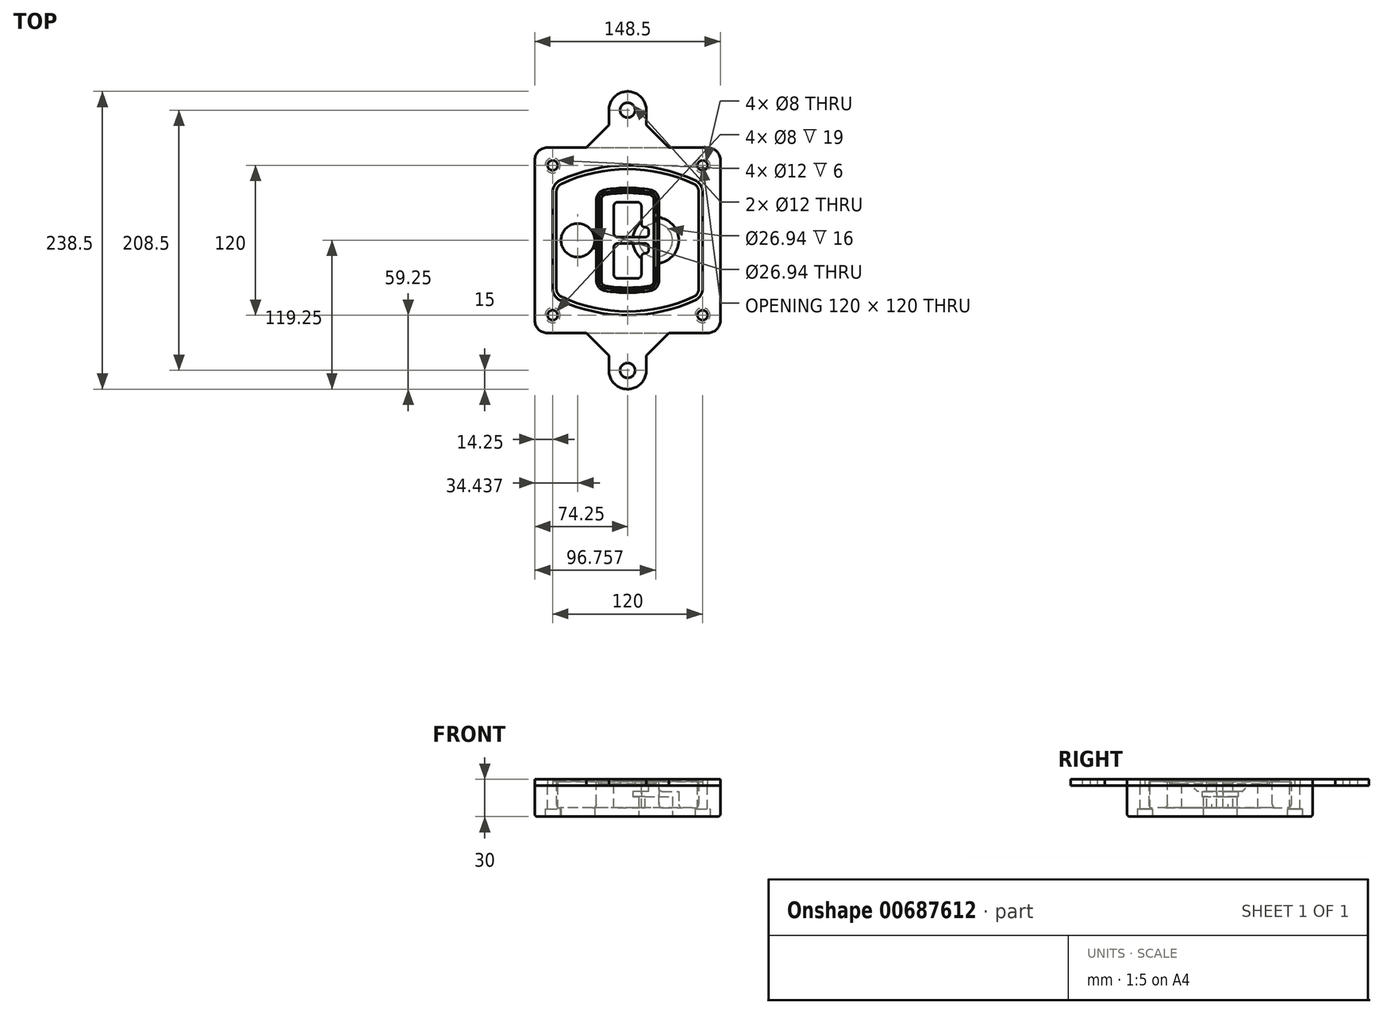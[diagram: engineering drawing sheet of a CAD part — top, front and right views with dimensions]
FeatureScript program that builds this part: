
annotation { "Feature Type Name" : "Feature", "Feature Type Description" : "" }
export const myFeature = defineFeature(function(context is Context, id is Id, definition is map)
    precondition{}
    {
        {
            var Q0;
            Q0=qCreatedBy(makeId("Top.planeOp"),FACE);
            var sketch = newSketch(context, id + "F0", { "sketchPlane" : qUnion([Q0])});
            skPoint(sketch, "E0.rect.middle", {"position": v(0, 0) * mm});
            skLineSegment(sketch, "E1.bottom", {"start": v(-64.25, -74.25) * mm, "end": v(64.25, -74.25) * mm});
            skLineSegment(sketch, "E1.top", {"start": v(-64.25, 74.25) * mm, "end": v(64.25, 74.25) * mm});
            skLineSegment(sketch, "E1.left", {"start": v(-74.25, -64.25) * mm, "end": v(-74.25, 64.25) * mm});
            skLineSegment(sketch, "E1.right", {"start": v(74.25, -64.25) * mm, "end": v(74.25, 64.25) * mm});
            skLineSegment(sketch, "E2", {"start": v(-74.25, 74.25) * mm, "end": v(74.25, -74.25) * mm, "construction": true});
            skLineSegment(sketch, "E3", {"start": v(74.25, 74.25) * mm, "end": v(-74.25, -74.25) * mm, "construction": true});
            skCircle(sketch, "E4", {"center": v(-60, 60) * mm, "radius": 4 * mm});
            skCircle(sketch, "E5", {"center": v(60, 60) * mm, "radius": 4 * mm});
            skCircle(sketch, "E6", {"center": v(60, -60) * mm, "radius": 4 * mm});
            skCircle(sketch, "E7", {"center": v(-60, -60) * mm, "radius": 4 * mm});
            skLineSegment(sketch, "E8", {"start": v(-60, 60) * mm, "end": v(60, 60) * mm, "construction": true});
            skLineSegment(sketch, "E9", {"start": v(60, 60) * mm, "end": v(60, -60) * mm, "construction": true});
            skLineSegment(sketch, "E10", {"start": v(60, -60) * mm, "end": v(-60, -60) * mm, "construction": true});
            skLineSegment(sketch, "E11", {"start": v(-60, -60) * mm, "end": v(-60, 60) * mm, "construction": true});
            skLineSegment(sketch, "E12", {"start": v(-60, 38.83) * mm, "end": v(-60, -38.83) * mm});
            skLineSegment(sketch, "E13", {"start": v(60, 38.83) * mm, "end": v(60, -38.83) * mm});
            skArc(sketch, "E14", {"start": v(54.26, 47.88) * mm, "mid": v(0, 60) * mm, "end": v(-54.26, 47.88) * mm});
            skArc(sketch, "E15", {"start": v(-54.26, -47.88) * mm, "mid": v(0, -60) * mm, "end": v(54.26, -47.88) * mm});
            skLineSegment(sketch, "E16", {"start": v(-60, 0) * mm, "end": v(60, 0) * mm, "construction": true});
            skPoint(sketch, "E17.visualSharp", {"position": v(-60, -45) * mm});
            skArc(sketch, "E17.filletArc", {"start": v(-60, -38.83) * mm, "mid": v(-58.44, -44.2) * mm, "end": v(-54.26, -47.88) * mm});
            skPoint(sketch, "E18.visualSharp", {"position": v(-60, 45) * mm});
            skArc(sketch, "E18.filletArc", {"start": v(-54.26, 47.88) * mm, "mid": v(-58.44, 44.2) * mm, "end": v(-60, 38.83) * mm});
            skPoint(sketch, "E19.visualSharp", {"position": v(60, 45) * mm});
            skArc(sketch, "E19.filletArc", {"start": v(60, 38.83) * mm, "mid": v(58.44, 44.2) * mm, "end": v(54.26, 47.88) * mm});
            skPoint(sketch, "E20.visualSharp", {"position": v(60, -45) * mm});
            skArc(sketch, "E20.filletArc", {"start": v(54.26, -47.88) * mm, "mid": v(58.44, -44.2) * mm, "end": v(60, -38.83) * mm});
            skPoint(sketch, "E21.visualSharp", {"position": v(-74.25, 74.25) * mm});
            skArc(sketch, "E21.filletArc", {"start": v(-64.25, 74.25) * mm, "mid": v(-71.32, 71.32) * mm, "end": v(-74.25, 64.25) * mm});
            skPoint(sketch, "E22.visualSharp", {"position": v(74.25, 74.25) * mm});
            skArc(sketch, "E22.filletArc", {"start": v(74.25, 64.25) * mm, "mid": v(71.32, 71.32) * mm, "end": v(64.25, 74.25) * mm});
            skPoint(sketch, "E23.visualSharp", {"position": v(74.25, -74.25) * mm});
            skArc(sketch, "E23.filletArc", {"start": v(64.25, -74.25) * mm, "mid": v(71.32, -71.32) * mm, "end": v(74.25, -64.25) * mm});
            skPoint(sketch, "E24.visualSharp", {"position": v(-74.25, -74.25) * mm});
            skArc(sketch, "E24.filletArc", {"start": v(-74.25, -64.25) * mm, "mid": v(-71.32, -71.32) * mm, "end": v(-64.25, -74.25) * mm});
            skArc(sketch, "E25.0", {"start": v(57, 38.83) * mm, "mid": v(55.9, 42.58) * mm, "end": v(52.98, 45.17) * mm});
            skLineSegment(sketch, "E25.1", {"start": v(57, 38.83) * mm, "end": v(57, -38.83) * mm});
            skArc(sketch, "E25.2", {"start": v(52.98, -45.17) * mm, "mid": v(55.9, -42.58) * mm, "end": v(57, -38.83) * mm});
            skArc(sketch, "E25.3", {"start": v(-52.98, -45.17) * mm, "mid": v(0, -57) * mm, "end": v(52.98, -45.17) * mm});
            skArc(sketch, "E25.4", {"start": v(-57, -38.83) * mm, "mid": v(-55.9, -42.58) * mm, "end": v(-52.98, -45.17) * mm});
            skArc(sketch, "E25.5", {"start": v(52.98, 45.17) * mm, "mid": v(0, 57) * mm, "end": v(-52.98, 45.17) * mm});
            skLineSegment(sketch, "E25.6", {"start": v(-57, 38.83) * mm, "end": v(-57, -38.83) * mm});
            skArc(sketch, "E25.7", {"start": v(-52.98, 45.17) * mm, "mid": v(-55.9, 42.58) * mm, "end": v(-57, 38.83) * mm});
            skArc(sketch, "E26.0", {"start": v(-55.96, 51.5) * mm, "mid": v(-61.82, 46.33) * mm, "end": v(-64, 38.83) * mm});
            skArc(sketch, "E26.1", {"start": v(55.96, 51.5) * mm, "mid": v(0, 64) * mm, "end": v(-55.96, 51.5) * mm});
            skArc(sketch, "E26.2", {"start": v(64, 38.83) * mm, "mid": v(61.82, 46.33) * mm, "end": v(55.96, 51.5) * mm});
            skLineSegment(sketch, "E26.3", {"start": v(64, 38.83) * mm, "end": v(64, -38.83) * mm});
            skArc(sketch, "E26.4", {"start": v(55.96, -51.5) * mm, "mid": v(61.82, -46.33) * mm, "end": v(64, -38.83) * mm});
            skLineSegment(sketch, "E26.5", {"start": v(-64, 38.83) * mm, "end": v(-64, -38.83) * mm});
            skArc(sketch, "E26.6", {"start": v(-55.96, -51.5) * mm, "mid": v(0, -64) * mm, "end": v(55.96, -51.5) * mm});
            skArc(sketch, "E26.7", {"start": v(-64, -38.83) * mm, "mid": v(-61.82, -46.33) * mm, "end": v(-55.96, -51.5) * mm});
            skSolve(sketch);
        }
        {
            var Q0;
            Q0=makeQuery(id+"F0.imprint","IMPRINT",FACE,{"disambiguationData":[TD([[makeQuery(id+"F0.imprint","IMPRINT",EDGE,{"derivedFrom":sQuery(id+"F0.wireOp",EDGE,"E1.bottom")}),1.0]])]});
            var Q1;
            Q1=makeQuery(id+"F0.imprint","IMPRINT",FACE,{"disambiguationData":[TD([[makeQuery(id+"F0.imprint","IMPRINT",EDGE,{"derivedFrom":sQuery(id+"F0.wireOp",EDGE,"E12")}),1.0]])]});
            var Q2;
            Q2=makeQuery(id+"F0.imprint","IMPRINT",FACE,{"disambiguationData":[TD([[makeQuery(id+"F0.imprint","IMPRINT",EDGE,{"derivedFrom":sQuery(id+"F0.wireOp",EDGE,"E25.0")}),1.0]])]});
            var Q3;
            Q3=makeQuery(id+"F0.imprint","IMPRINT",FACE,{"disambiguationData":[TD([[makeQuery(id+"F0.imprint","IMPRINT",EDGE,{"derivedFrom":sQuery(id+"F0.wireOp",EDGE,"E12")}),-1.0]])]});
            extrude(context, id + "F1", {"entities" : qUnion([Q0, Q1, Q2, Q3]), "oppositeDirection" : true, "depth" : 25 * mm});
        }
        {
            var Q0;
            Q0=makeQuery(id+"F0.imprint","IMPRINT",FACE,{"disambiguationData":[TD([[makeQuery(id+"F0.imprint","IMPRINT",EDGE,{"derivedFrom":sQuery(id+"F0.wireOp",EDGE,"E12")}),1.0]])]});
            extrude(context, id + "F2", {"entities" : qUnion([Q0]), "operationType" : NewBodyOperationType.ADD, "depth" : 3 * mm});
        }
        {
            var Q0;
            Q0=makeQuery(id+"F0.imprint","IMPRINT",FACE,{"disambiguationData":[TD([[makeQuery(id+"F0.imprint","IMPRINT",EDGE,{"derivedFrom":sQuery(id+"F0.wireOp",EDGE,"E25.0")}),1.0]])]});
            extrude(context, id + "F3", {"entities" : qUnion([Q0]), "operationType" : NewBodyOperationType.REMOVE, "oppositeDirection" : true, "depth" : 18 * mm});
        }
        {
            var Q0;
            Q0=makeQuery(id+"F2.opExtrude","CAP_FACE",FACE,{"disambiguationData":[OSD([sQuery(id+"F0.wireOp",EDGE,"E12"),sQuery(id+"F0.wireOp",EDGE,"E13"),sQuery(id+"F0.wireOp",EDGE,"E14"),sQuery(id+"F0.wireOp",EDGE,"E15"),sQuery(id+"F0.wireOp",EDGE,"E17.filletArc"),sQuery(id+"F0.wireOp",EDGE,"E18.filletArc"),sQuery(id+"F0.wireOp",EDGE,"E19.filletArc"),sQuery(id+"F0.wireOp",EDGE,"E20.filletArc"),sQuery(id+"F0.wireOp",EDGE,"E25.0"),sQuery(id+"F0.wireOp",EDGE,"E25.1"),sQuery(id+"F0.wireOp",EDGE,"E25.2"),sQuery(id+"F0.wireOp",EDGE,"E25.3"),sQuery(id+"F0.wireOp",EDGE,"E25.4"),sQuery(id+"F0.wireOp",EDGE,"E25.5"),sQuery(id+"F0.wireOp",EDGE,"E25.6"),sQuery(id+"F0.wireOp",EDGE,"E25.7")])],"isStart":false});
            var sketch = newSketch(context, id + "F4", { "sketchPlane" : qUnion([Q0])});
            skArc(sketch, "E27.0", {"start": v(-18.34, -40.45) * mm, "mid": v(0, -42) * mm, "end": v(18.34, -40.45) * mm});
            skArc(sketch, "E28.0", {"start": v(18.34, 40.45) * mm, "mid": v(0, 42) * mm, "end": v(-18.34, 40.45) * mm});
            skLineSegment(sketch, "E29", {"start": v(-25, 32.57) * mm, "end": v(-25, -32.57) * mm});
            skLineSegment(sketch, "E30", {"start": v(25, 32.57) * mm, "end": v(25, -32.57) * mm});
            skLineSegment(sketch, "E31", {"start": v(-25, 39.1) * mm, "end": v(25, 39.1) * mm, "construction": true});
            skLineSegment(sketch, "E32", {"start": v(-25, -39.1) * mm, "end": v(25, -39.1) * mm, "construction": true});
            skPoint(sketch, "E33.visualSharp", {"position": v(-25, 39.1) * mm});
            skArc(sketch, "E33.filletArc", {"start": v(-18.34, 40.45) * mm, "mid": v(-23.11, 37.73) * mm, "end": v(-25, 32.57) * mm});
            skPoint(sketch, "E34.visualSharp", {"position": v(25, 39.1) * mm});
            skArc(sketch, "E34.filletArc", {"start": v(25, 32.57) * mm, "mid": v(23.11, 37.73) * mm, "end": v(18.34, 40.45) * mm});
            skPoint(sketch, "E35.visualSharp", {"position": v(25, -39.1) * mm});
            skArc(sketch, "E35.filletArc", {"start": v(18.34, -40.45) * mm, "mid": v(23.11, -37.73) * mm, "end": v(25, -32.57) * mm});
            skPoint(sketch, "E36.visualSharp", {"position": v(-25, -39.1) * mm});
            skArc(sketch, "E36.filletArc", {"start": v(-25, -32.57) * mm, "mid": v(-23.11, -37.73) * mm, "end": v(-18.34, -40.45) * mm});
            skArc(sketch, "E37.0", {"start": v(52.98, 45.17) * mm, "mid": v(0, 57) * mm, "end": v(-52.98, 45.17) * mm});
            skArc(sketch, "E37.1", {"start": v(-52.98, 45.17) * mm, "mid": v(-55.9, 42.58) * mm, "end": v(-57, 38.83) * mm});
            skLineSegment(sketch, "E37.2", {"start": v(-57, 38.83) * mm, "end": v(-57, -38.83) * mm});
            skArc(sketch, "E37.3", {"start": v(-57, -38.83) * mm, "mid": v(-55.9, -42.58) * mm, "end": v(-52.98, -45.17) * mm});
            skArc(sketch, "E37.4", {"start": v(-52.98, -45.17) * mm, "mid": v(0, -57) * mm, "end": v(52.98, -45.17) * mm});
            skArc(sketch, "E37.5", {"start": v(52.98, -45.17) * mm, "mid": v(55.9, -42.58) * mm, "end": v(57, -38.83) * mm});
            skLineSegment(sketch, "E37.6", {"start": v(57, 38.83) * mm, "end": v(57, -38.83) * mm});
            skArc(sketch, "E37.7", {"start": v(57, 38.83) * mm, "mid": v(55.9, 42.58) * mm, "end": v(52.98, 45.17) * mm});
            skLineSegment(sketch, "E38.0", {"start": v(23, 32.57) * mm, "end": v(23, -32.57) * mm});
            skArc(sketch, "E38.1", {"start": v(18, -38.48) * mm, "mid": v(21.58, -36.44) * mm, "end": v(23, -32.57) * mm});
            skArc(sketch, "E38.2", {"start": v(-18, -38.48) * mm, "mid": v(0, -40) * mm, "end": v(18, -38.48) * mm});
            skArc(sketch, "E38.3", {"start": v(-23, -32.57) * mm, "mid": v(-21.58, -36.44) * mm, "end": v(-18, -38.48) * mm});
            skLineSegment(sketch, "E38.4", {"start": v(-23, 32.57) * mm, "end": v(-23, -32.57) * mm});
            skArc(sketch, "E38.5", {"start": v(23, 32.57) * mm, "mid": v(21.58, 36.44) * mm, "end": v(18, 38.48) * mm});
            skArc(sketch, "E38.6", {"start": v(-18, 38.48) * mm, "mid": v(-21.58, 36.44) * mm, "end": v(-23, 32.57) * mm});
            skArc(sketch, "E38.7", {"start": v(18, 38.48) * mm, "mid": v(0, 40) * mm, "end": v(-18, 38.48) * mm});
            skArc(sketch, "E39.0", {"start": v(21, 32.57) * mm, "mid": v(20.06, 35.15) * mm, "end": v(17.67, 36.5) * mm});
            skLineSegment(sketch, "E39.1", {"start": v(21, 32.57) * mm, "end": v(21, -32.57) * mm});
            skArc(sketch, "E39.2", {"start": v(17.67, -36.5) * mm, "mid": v(20.06, -35.15) * mm, "end": v(21, -32.57) * mm});
            skArc(sketch, "E39.3", {"start": v(-17.67, -36.5) * mm, "mid": v(0, -38) * mm, "end": v(17.67, -36.5) * mm});
            skArc(sketch, "E39.4", {"start": v(-21, -32.57) * mm, "mid": v(-20.06, -35.15) * mm, "end": v(-17.67, -36.5) * mm});
            skArc(sketch, "E39.5", {"start": v(17.67, 36.5) * mm, "mid": v(0, 38) * mm, "end": v(-17.67, 36.5) * mm});
            skLineSegment(sketch, "E39.6", {"start": v(-21, 32.57) * mm, "end": v(-21, -32.57) * mm});
            skArc(sketch, "E39.7", {"start": v(-17.67, 36.5) * mm, "mid": v(-20.06, 35.15) * mm, "end": v(-21, 32.57) * mm});
            skLineSegment(sketch, "E40", {"start": v(-25, 0) * mm, "end": v(25, 0) * mm, "construction": true});
            skLineSegment(sketch, "E41", {"start": v(-11, 5.5) * mm, "end": v(-11, 27.5) * mm});
            skLineSegment(sketch, "E42", {"start": v(-8, 30.5) * mm, "end": v(8, 30.5) * mm});
            skLineSegment(sketch, "E43", {"start": v(11, 27.5) * mm, "end": v(11, 13.5) * mm});
            skLineSegment(sketch, "E44", {"start": v(14, 10.5) * mm, "end": v(14, 10.5) * mm});
            skLineSegment(sketch, "E45", {"start": v(17, 7.5) * mm, "end": v(17, 5.5) * mm});
            skLineSegment(sketch, "E46", {"start": v(14, 2.5) * mm, "end": v(-8, 2.5) * mm});
            skPoint(sketch, "E47.visualSharp", {"position": v(-11, 30.5) * mm});
            skArc(sketch, "E47.filletArc", {"start": v(-8, 30.5) * mm, "mid": v(-10.12, 29.62) * mm, "end": v(-11, 27.5) * mm});
            skPoint(sketch, "E48.visualSharp", {"position": v(11, 30.5) * mm});
            skArc(sketch, "E48.filletArc", {"start": v(11, 27.5) * mm, "mid": v(10.12, 29.62) * mm, "end": v(8, 30.5) * mm});
            skPoint(sketch, "E49.visualSharp", {"position": v(11, 10.5) * mm});
            skArc(sketch, "E49.filletArc", {"start": v(11, 13.5) * mm, "mid": v(11.88, 11.38) * mm, "end": v(14, 10.5) * mm});
            skPoint(sketch, "E50.visualSharp", {"position": v(17, 10.5) * mm});
            skArc(sketch, "E50.filletArc", {"start": v(17, 7.5) * mm, "mid": v(16.12, 9.62) * mm, "end": v(14, 10.5) * mm});
            skPoint(sketch, "E51.visualSharp", {"position": v(17, 2.5) * mm});
            skArc(sketch, "E51.filletArc", {"start": v(14, 2.5) * mm, "mid": v(16.12, 3.38) * mm, "end": v(17, 5.5) * mm});
            skPoint(sketch, "E52.visualSharp", {"position": v(-11, 2.5) * mm});
            skArc(sketch, "E52.filletArc", {"start": v(-11, 5.5) * mm, "mid": v(-10.12, 3.38) * mm, "end": v(-8, 2.5) * mm});
            skLineSegment(sketch, "E53.0.MirrorCS", {"start": v(14, -2.5) * mm, "end": v(-8, -2.5) * mm});
            skArc(sketch, "E54.0.MirrorCS", {"start": v(-11, -5.5) * mm, "mid": v(-10.12, -3.38) * mm, "end": v(-8, -2.5) * mm});
            skLineSegment(sketch, "E55.0.MirrorCS", {"start": v(-11, -5.5) * mm, "end": v(-11, -27.5) * mm});
            skArc(sketch, "E56.0.MirrorCS", {"start": v(-8, -30.5) * mm, "mid": v(-10.12, -29.62) * mm, "end": v(-11, -27.5) * mm});
            skLineSegment(sketch, "E57.0.MirrorCS", {"start": v(-8, -30.5) * mm, "end": v(8, -30.5) * mm});
            skArc(sketch, "E58.0.MirrorCS", {"start": v(11, -27.5) * mm, "mid": v(10.12, -29.62) * mm, "end": v(8, -30.5) * mm});
            skLineSegment(sketch, "E59.0.MirrorCS", {"start": v(11, -27.5) * mm, "end": v(11, -13.5) * mm});
            skArc(sketch, "E60.0.MirrorCS", {"start": v(11, -13.5) * mm, "mid": v(11.88, -11.38) * mm, "end": v(14, -10.5) * mm});
            skArc(sketch, "E61.0.MirrorCS", {"start": v(17, -7.5) * mm, "mid": v(16.12, -9.62) * mm, "end": v(14, -10.5) * mm});
            skLineSegment(sketch, "E62.0.MirrorCS", {"start": v(17, -7.5) * mm, "end": v(17, -5.5) * mm});
            skArc(sketch, "E63.0.MirrorCS", {"start": v(14, -2.5) * mm, "mid": v(16.12, -3.38) * mm, "end": v(17, -5.5) * mm});
            skSolve(sketch);
        }
        {
            var Q0;
            Q0=makeQuery(id+"F4.imprint","IMPRINT",FACE,{"disambiguationData":[TD([[makeQuery(id+"F4.imprint","IMPRINT",EDGE,{"derivedFrom":sQuery(id+"F4.wireOp",EDGE,"E27.0")}),1.0]])]});
            var Q1;
            Q1=makeQuery(id+"F4.imprint","IMPRINT",FACE,{"disambiguationData":[TD([[makeQuery(id+"F4.imprint","IMPRINT",EDGE,{"derivedFrom":sQuery(id+"F4.wireOp",EDGE,"E38.0")}),-1.0]])]});
            var Q2;
            Q2=makeQuery(id+"F4.imprint","IMPRINT",FACE,{"disambiguationData":[TD([[makeQuery(id+"F4.imprint","IMPRINT",EDGE,{"derivedFrom":sQuery(id+"F4.wireOp",EDGE,"E39.0")}),1.0]])]});
            extrude(context, id + "F5", {"entities" : qUnion([Q0, Q1, Q2]), "operationType" : NewBodyOperationType.ADD, "endBound" : BoundingType.UP_TO_NEXT, "oppositeDirection" : true, "depth" : 25 * mm});
        }
        {
            var Q0;
            Q0=makeQuery(id+"F4.imprint","IMPRINT",FACE,{"disambiguationData":[TD([[makeQuery(id+"F4.imprint","IMPRINT",EDGE,{"derivedFrom":sQuery(id+"F4.wireOp",EDGE,"E38.0")}),-1.0]])]});
            extrude(context, id + "F6", {"entities" : qUnion([Q0]), "operationType" : NewBodyOperationType.REMOVE, "oppositeDirection" : true, "depth" : 2 * mm});
        }
        {
            var Q0;
            Q0=makeQuery(id+"F1.opExtrude","CAP_FACE",FACE,{"disambiguationData":[OSD([sQuery(id+"F0.wireOp",EDGE,"E1.bottom"),sQuery(id+"F0.wireOp",EDGE,"E1.top"),sQuery(id+"F0.wireOp",EDGE,"E1.left"),sQuery(id+"F0.wireOp",EDGE,"E1.right"),sQuery(id+"F0.wireOp",EDGE,"E4"),sQuery(id+"F0.wireOp",EDGE,"E5"),sQuery(id+"F0.wireOp",EDGE,"E6"),sQuery(id+"F0.wireOp",EDGE,"E7"),sQuery(id+"F0.wireOp",EDGE,"E21.filletArc"),sQuery(id+"F0.wireOp",EDGE,"E22.filletArc"),sQuery(id+"F0.wireOp",EDGE,"E23.filletArc"),sQuery(id+"F0.wireOp",EDGE,"E24.filletArc")])],"isStart":false});
            var sketch = newSketch(context, id + "F7", { "sketchPlane" : qUnion([Q0])});
            skCircle(sketch, "E64", {"center": v(22.5, 0) * mm, "radius": 13.47 * mm});
            skCircle(sketch, "E65", {"center": v(-39.81, 0) * mm, "radius": 13.47 * mm});
            skLineSegment(sketch, "E66", {"start": v(74.25, 0) * mm, "end": v(-74.25, 0) * mm});
            skCircle(sketch, "E67", {"center": v(22.5, 0) * mm, "radius": 18.47 * mm});
            skCircle(sketch, "E68", {"center": v(60, -60) * mm, "radius": 6 * mm});
            skCircle(sketch, "E69", {"center": v(-60, -60) * mm, "radius": 6 * mm});
            skCircle(sketch, "E70", {"center": v(-60, 60) * mm, "radius": 6 * mm});
            skCircle(sketch, "E71", {"center": v(60, 60) * mm, "radius": 6 * mm});
            skSolve(sketch);
        }
        {
            var Q0;
            {var subQ1=sQuery(id+"F7.wireOp",EDGE,"E66");var subQ4=sQuery(id+"F7.wireOp",EDGE,"E64");var subQ6=makeQuery(id+"F7.imprint","INTERSECT",VERTEX,{"disambiguationData":[OD(0.0)],"derivedFrom":[subQ4,subQ1]});Q0=makeQuery(id+"F7.imprint","IMPRINT",FACE,{"disambiguationData":[TD([[makeQuery(id+"F7.imprint","IMPRINT",EDGE,{"disambiguationData":[TD([[subQ6,-1.0]])],"derivedFrom":subQ4}),-1.0]])]});}
            var Q1;
            {var subQ0=sQuery(id+"F7.wireOp",EDGE,"E66");var subQ1=sQuery(id+"F7.wireOp",EDGE,"E64");var subQ3=makeQuery(id+"F7.imprint","INTERSECT",VERTEX,{"disambiguationData":[OD(0.0)],"derivedFrom":[subQ1,subQ0]});Q1=makeQuery(id+"F7.imprint","IMPRINT",FACE,{"disambiguationData":[TD([[makeQuery(id+"F7.imprint","IMPRINT",EDGE,{"disambiguationData":[TD([[subQ3,-1.0]])],"derivedFrom":subQ1}),1.0]])]});}
            var Q2;
            {var subQ0=sQuery(id+"F7.wireOp",EDGE,"E66");var subQ1=sQuery(id+"F7.wireOp",EDGE,"E64");var subQ3=makeQuery(id+"F7.imprint","INTERSECT",VERTEX,{"disambiguationData":[OD(0.0)],"derivedFrom":[subQ1,subQ0]});Q2=makeQuery(id+"F7.imprint","IMPRINT",FACE,{"disambiguationData":[TD([[makeQuery(id+"F7.imprint","IMPRINT",EDGE,{"disambiguationData":[TD([[subQ3,1.0]])],"derivedFrom":subQ1}),1.0]])]});}
            var Q3;
            {var subQ1=sQuery(id+"F7.wireOp",EDGE,"E66");var subQ4=sQuery(id+"F7.wireOp",EDGE,"E64");var subQ6=makeQuery(id+"F7.imprint","INTERSECT",VERTEX,{"disambiguationData":[OD(0.0)],"derivedFrom":[subQ4,subQ1]});Q3=makeQuery(id+"F7.imprint","IMPRINT",FACE,{"disambiguationData":[TD([[makeQuery(id+"F7.imprint","IMPRINT",EDGE,{"disambiguationData":[TD([[subQ6,1.0]])],"derivedFrom":subQ4}),-1.0]])]});}
            extrude(context, id + "F8", {"entities" : qUnion([Q0, Q1, Q2, Q3]), "operationType" : NewBodyOperationType.ADD, "oppositeDirection" : true, "depth" : 20 * mm});
        }
        {
            var Q0;
            {var subQ0=sQuery(id+"F7.wireOp",EDGE,"E66");var subQ1=sQuery(id+"F7.wireOp",EDGE,"E64");var subQ3=makeQuery(id+"F7.imprint","INTERSECT",VERTEX,{"disambiguationData":[OD(0.0)],"derivedFrom":[subQ1,subQ0]});Q0=makeQuery(id+"F7.imprint","IMPRINT",FACE,{"disambiguationData":[TD([[makeQuery(id+"F7.imprint","IMPRINT",EDGE,{"disambiguationData":[TD([[subQ3,-1.0]])],"derivedFrom":subQ1}),1.0]])]});}
            var Q1;
            {var subQ0=sQuery(id+"F7.wireOp",EDGE,"E66");var subQ1=sQuery(id+"F7.wireOp",EDGE,"E64");var subQ3=makeQuery(id+"F7.imprint","INTERSECT",VERTEX,{"disambiguationData":[OD(0.0)],"derivedFrom":[subQ1,subQ0]});Q1=makeQuery(id+"F7.imprint","IMPRINT",FACE,{"disambiguationData":[TD([[makeQuery(id+"F7.imprint","IMPRINT",EDGE,{"disambiguationData":[TD([[subQ3,1.0]])],"derivedFrom":subQ1}),1.0]])]});}
            extrude(context, id + "F9", {"entities" : qUnion([Q0, Q1]), "operationType" : NewBodyOperationType.REMOVE, "oppositeDirection" : true, "depth" : 16 * mm});
        }
        {
            var Q0;
            {var subQ0=sQuery(id+"F7.wireOp",EDGE,"E66");var subQ1=sQuery(id+"F7.wireOp",EDGE,"E65");var subQ3=makeQuery(id+"F7.imprint","INTERSECT",VERTEX,{"disambiguationData":[OD(0.0)],"derivedFrom":[subQ1,subQ0]});Q0=makeQuery(id+"F7.imprint","IMPRINT",FACE,{"disambiguationData":[TD([[makeQuery(id+"F7.imprint","IMPRINT",EDGE,{"disambiguationData":[TD([[subQ3,-1.0]])],"derivedFrom":subQ1}),1.0]])]});}
            var Q1;
            {var subQ0=sQuery(id+"F7.wireOp",EDGE,"E66");var subQ1=sQuery(id+"F7.wireOp",EDGE,"E65");var subQ3=makeQuery(id+"F7.imprint","INTERSECT",VERTEX,{"disambiguationData":[OD(0.0)],"derivedFrom":[subQ1,subQ0]});Q1=makeQuery(id+"F7.imprint","IMPRINT",FACE,{"disambiguationData":[TD([[makeQuery(id+"F7.imprint","IMPRINT",EDGE,{"disambiguationData":[TD([[subQ3,1.0]])],"derivedFrom":subQ1}),1.0]])]});}
            extrude(context, id + "F10", {"entities" : qUnion([Q0, Q1]), "operationType" : NewBodyOperationType.REMOVE, "oppositeDirection" : true, "depth" : 25 * mm});
        }
        {
            var Q0;
            Q0=makeQuery(id+"F7.imprint","IMPRINT",FACE,{"disambiguationData":[TD([[makeQuery(id+"F7.imprint","IMPRINT",EDGE,{"derivedFrom":sQuery(id+"F7.wireOp",EDGE,"E68")}),1.0]])]});
            var Q1;
            Q1=makeQuery(id+"F7.imprint","IMPRINT",FACE,{"disambiguationData":[TD([[makeQuery(id+"F7.imprint","IMPRINT",EDGE,{"derivedFrom":makeQuery(id+"F1.opExtrude","CAP_EDGE",EDGE,{"disambiguationData":[OSD([sQuery(id+"F0.wireOp",EDGE,"E5")])],"isStart":false})}),-1.0]])]});
            var Q2;
            Q2=makeQuery(id+"F7.imprint","IMPRINT",FACE,{"disambiguationData":[TD([[makeQuery(id+"F7.imprint","IMPRINT",EDGE,{"derivedFrom":sQuery(id+"F7.wireOp",EDGE,"E69")}),1.0]])]});
            var Q3;
            Q3=makeQuery(id+"F7.imprint","IMPRINT",FACE,{"disambiguationData":[TD([[makeQuery(id+"F7.imprint","IMPRINT",EDGE,{"derivedFrom":makeQuery(id+"F1.opExtrude","CAP_EDGE",EDGE,{"disambiguationData":[OSD([sQuery(id+"F0.wireOp",EDGE,"E4")])],"isStart":false})}),-1.0]])]});
            var Q4;
            Q4=makeQuery(id+"F7.imprint","IMPRINT",FACE,{"disambiguationData":[TD([[makeQuery(id+"F7.imprint","IMPRINT",EDGE,{"derivedFrom":sQuery(id+"F7.wireOp",EDGE,"E70")}),1.0]])]});
            var Q5;
            Q5=makeQuery(id+"F7.imprint","IMPRINT",FACE,{"disambiguationData":[TD([[makeQuery(id+"F7.imprint","IMPRINT",EDGE,{"derivedFrom":makeQuery(id+"F1.opExtrude","CAP_EDGE",EDGE,{"disambiguationData":[OSD([sQuery(id+"F0.wireOp",EDGE,"E7")])],"isStart":false})}),-1.0]])]});
            var Q6;
            Q6=makeQuery(id+"F7.imprint","IMPRINT",FACE,{"disambiguationData":[TD([[makeQuery(id+"F7.imprint","IMPRINT",EDGE,{"derivedFrom":sQuery(id+"F7.wireOp",EDGE,"E71")}),1.0]])]});
            var Q7;
            Q7=makeQuery(id+"F7.imprint","IMPRINT",FACE,{"disambiguationData":[TD([[makeQuery(id+"F7.imprint","IMPRINT",EDGE,{"derivedFrom":makeQuery(id+"F1.opExtrude","CAP_EDGE",EDGE,{"disambiguationData":[OSD([sQuery(id+"F0.wireOp",EDGE,"E6")])],"isStart":false})}),-1.0]])]});
            extrude(context, id + "F11", {"entities" : qUnion([Q0, Q1, Q2, Q3, Q4, Q5, Q6, Q7]), "operationType" : NewBodyOperationType.REMOVE, "oppositeDirection" : true, "depth" : 6 * mm});
        }
        {
            var Q0;
            Q0=makeQuery(id+"F9.boolean.opBoolean","COPY",FACE,{"derivedFrom":makeQuery(id+"F9.opExtrude","CAP_FACE",FACE,{"disambiguationData":[OSD([sQuery(id+"F7.wireOp",EDGE,"E64")])],"isStart":false})});
            var sketch = newSketch(context, id + "F12", { "sketchPlane" : qUnion([Q0])});
            skArc(sketch, "E72.0", {"start": v(11, 14.45) * mm, "mid": v(6.45, 9.13) * mm, "end": v(4.2, 2.5) * mm});
            skArc(sketch, "E72.1", {"start": v(4.2, -2.5) * mm, "mid": v(6.45, -9.13) * mm, "end": v(11, -14.45) * mm});
            skLineSegment(sketch, "E73", {"start": v(4.2, -2.5) * mm, "end": v(14, -2.5) * mm});
            skLineSegment(sketch, "E74.0", {"start": v(14, 2.5) * mm, "end": v(4.2, 2.5) * mm});
            skArc(sketch, "E74.1", {"start": v(14, 2.5) * mm, "mid": v(16.12, 3.38) * mm, "end": v(17, 5.5) * mm});
            skLineSegment(sketch, "E74.2", {"start": v(17, 7.5) * mm, "end": v(17, 5.5) * mm});
            skArc(sketch, "E74.3", {"start": v(17, 7.5) * mm, "mid": v(16.12, 9.62) * mm, "end": v(14, 10.5) * mm});
            skArc(sketch, "E74.4", {"start": v(11, 13.5) * mm, "mid": v(11.88, 11.38) * mm, "end": v(14, 10.5) * mm});
            skLineSegment(sketch, "E74.5", {"start": v(11, 14.45) * mm, "end": v(11, 13.5) * mm});
            skLineSegment(sketch, "E74.7", {"start": v(14, -2.5) * mm, "end": v(4.2, -2.5) * mm});
            skArc(sketch, "E74.8", {"start": v(14, -2.5) * mm, "mid": v(16.12, -3.38) * mm, "end": v(17, -5.5) * mm});
            skLineSegment(sketch, "E74.9", {"start": v(17, -7.5) * mm, "end": v(17, -5.5) * mm});
            skArc(sketch, "E74.10", {"start": v(17, -7.5) * mm, "mid": v(16.12, -9.62) * mm, "end": v(14, -10.5) * mm});
            skArc(sketch, "E74.11", {"start": v(11, -13.5) * mm, "mid": v(11.88, -11.38) * mm, "end": v(14, -10.5) * mm});
            skLineSegment(sketch, "E74.12", {"start": v(11, -14.45) * mm, "end": v(11, -13.5) * mm});
            skPoint(sketch, "E75.orphan", {"position": v(11, -27.5) * mm});
            skPoint(sketch, "E76.orphan", {"position": v(-8, -2.5) * mm});
            skPoint(sketch, "E77.orphan", {"position": v(-8, 2.5) * mm});
            skPoint(sketch, "E78.orphan", {"position": v(11, 27.5) * mm});
            skSolve(sketch);
        }
        {
            var Q0;
            {var subQ7=sQuery(id+"F12.wireOp",EDGE,"E72.0");var subQ14=sQuery(id+"F12.wireOp",EDGE,"E72.1");var subQ16=sQuery(id+"F12.wireOp",EDGE,"E74.1");var subQ18=sQuery(id+"F12.wireOp",EDGE,"E74.8");Q0=qUnion([makeQuery(id+"F12.imprint","IMPRINT",FACE,{"disambiguationData":[TD([[makeQuery(id+"F12.imprint","IMPRINT",EDGE,{"derivedFrom":subQ7}),1.0]])]}),makeQuery(id+"F12.imprint","IMPRINT",FACE,{"disambiguationData":[TD([[makeQuery(id+"F12.imprint","IMPRINT",EDGE,{"derivedFrom":subQ14}),1.0]])]}),makeQuery(id+"F12.imprint","IMPRINT",FACE,{"disambiguationData":[TD([[makeQuery(id+"F12.imprint","IMPRINT",EDGE,{"derivedFrom":subQ16}),1.0]])]}),makeQuery(id+"F12.imprint","IMPRINT",FACE,{"disambiguationData":[TD([[makeQuery(id+"F12.imprint","IMPRINT",EDGE,{"derivedFrom":subQ18}),-1.0]])]})]);}
            var Q1;
            Q1=makeQuery(id+"F5.boolean.opBoolean","SPLIT",FACE,{"disambiguationData":[TD([makeQuery(id+"F5.opExtrude","SWEPT_FACE",FACE,{"disambiguationData":[OSD([sQuery(id+"F4.wireOp",EDGE,"E41")])]})])],"derivedFrom":makeQuery(id+"F3.boolean.opBoolean","COPY",FACE,{"derivedFrom":makeQuery(id+"F3.opExtrude","CAP_FACE",FACE,{"disambiguationData":[OSD([sQuery(id+"F0.wireOp",EDGE,"E25.0"),sQuery(id+"F0.wireOp",EDGE,"E25.1"),sQuery(id+"F0.wireOp",EDGE,"E25.2"),sQuery(id+"F0.wireOp",EDGE,"E25.3"),sQuery(id+"F0.wireOp",EDGE,"E25.4"),sQuery(id+"F0.wireOp",EDGE,"E25.5"),sQuery(id+"F0.wireOp",EDGE,"E25.6"),sQuery(id+"F0.wireOp",EDGE,"E25.7")])],"isStart":false})})});
            extrude(context, id + "F13", {"entities" : qUnion([Q0]), "operationType" : NewBodyOperationType.REMOVE, "endBound" : BoundingType.UP_TO_SURFACE, "endBoundEntityFace" : qUnion([Q1]), "depth" : 25 * mm});
        }
        {
            var Q0;
            Q0=makeQuery(id+"F3.boolean.opBoolean","COPY",EDGE,{"derivedFrom":makeQuery(id+"F3.opExtrude","CAP_EDGE",EDGE,{"disambiguationData":[OSD([sQuery(id+"F0.wireOp",EDGE,"E25.6")])],"isStart":false})});
            var Q1;
            Q1=makeQuery(id+"F8.boolean.opBoolean","INTERSECT",EDGE,{"derivedFrom":[makeQuery(id+"F5.opExtrude","SWEPT_FACE",FACE,{"disambiguationData":[OSD([sQuery(id+"F4.wireOp",EDGE,"E30")])]}),makeQuery(id+"F8.opExtrude","CAP_FACE",FACE,{"disambiguationData":[OSD([sQuery(id+"F7.wireOp",EDGE,"E67")])],"isStart":false})]});
            var Q2;
            Q2=makeQuery(id+"F8.boolean.opBoolean","INTERSECT",EDGE,{"disambiguationData":[OD(1.0)],"derivedFrom":[makeQuery(id+"F5.opExtrude","SWEPT_FACE",FACE,{"disambiguationData":[OSD([sQuery(id+"F4.wireOp",EDGE,"E30")])]}),makeQuery(id+"F8.opExtrude","SWEPT_FACE",FACE,{"disambiguationData":[OSD([sQuery(id+"F7.wireOp",EDGE,"E67")])]})]});
            var Q3;
            {var subQ0=sQuery(id+"F4.wireOp",EDGE,"E30");Q3=makeQuery(id+"F8.boolean.opBoolean","SPLIT",EDGE,{"disambiguationData":[TD([makeQuery(id+"F5.opExtrude","SWEPT_FACE",FACE,{"disambiguationData":[OSD([sQuery(id+"F4.wireOp",EDGE,"E35.filletArc")])]})])],"derivedFrom":makeQuery(id+"F5.opExtrude","CAP_EDGE",EDGE,{"disambiguationData":[OSD([subQ0])],"isStart":false})});}
            var Q4;
            {var subQ0=sQuery(id+"F0.wireOp",EDGE,"E25.7");var subQ1=sQuery(id+"F0.wireOp",EDGE,"E25.1");var subQ2=sQuery(id+"F0.wireOp",EDGE,"E25.6");var subQ3=sQuery(id+"F0.wireOp",EDGE,"E25.5");var subQ4=sQuery(id+"F0.wireOp",EDGE,"E25.4");var subQ5=sQuery(id+"F0.wireOp",EDGE,"E25.0");var subQ6=sQuery(id+"F0.wireOp",EDGE,"E25.2");var subQ7=sQuery(id+"F0.wireOp",EDGE,"E25.3");Q4=makeQuery(id+"F8.boolean.opBoolean","INTERSECT",EDGE,{"derivedFrom":[makeQuery(id+"F5.boolean.opBoolean","SPLIT",FACE,{"disambiguationData":[TD([makeQuery(id+"F2.opExtrude","SWEPT_FACE",FACE,{"disambiguationData":[OSD([subQ5])]})])],"derivedFrom":makeQuery(id+"F3.boolean.opBoolean","COPY",FACE,{"derivedFrom":makeQuery(id+"F3.opExtrude","CAP_FACE",FACE,{"disambiguationData":[OSD([subQ5,subQ1,subQ6,subQ7,subQ4,subQ3,subQ2,subQ0])],"isStart":false})})}),makeQuery(id+"F8.opExtrude","SWEPT_FACE",FACE,{"disambiguationData":[OSD([sQuery(id+"F7.wireOp",EDGE,"E67")])]})]});}
            var Q5;
            Q5=makeQuery(id+"F8.boolean.opBoolean","INTERSECT",EDGE,{"disambiguationData":[OD(0.0)],"derivedFrom":[makeQuery(id+"F5.opExtrude","SWEPT_FACE",FACE,{"disambiguationData":[OSD([sQuery(id+"F4.wireOp",EDGE,"E30")])]}),makeQuery(id+"F8.opExtrude","SWEPT_FACE",FACE,{"disambiguationData":[OSD([sQuery(id+"F7.wireOp",EDGE,"E67")])]})]});
            fillet(context, id + "F14", {"entities" : qUnion([Q0, Q1, Q2, Q3, Q4, Q5]), "radius" : 3 * mm, "tangentPropagation" : true, "allowEdgeOverflow" : false});
        }
        {
            var Q0;
            Q0=makeQuery(id+"F1.opExtrude","CAP_EDGE",EDGE,{"disambiguationData":[OSD([sQuery(id+"F0.wireOp",EDGE,"E1.bottom")])],"isStart":false});
            fillet(context, id + "F15", {"entities" : qUnion([Q0]), "radius" : 2 * mm, "tangentPropagation" : true, "allowEdgeOverflow" : false});
        }
        {
            var Q0;
            {var subQ0=sQuery(id+"F0.wireOp",EDGE,"E21.filletArc");var subQ1=sQuery(id+"F0.wireOp",EDGE,"E7");var subQ2=sQuery(id+"F0.wireOp",EDGE,"E6");var subQ3=sQuery(id+"F0.wireOp",EDGE,"E5");var subQ4=sQuery(id+"F0.wireOp",EDGE,"E4");var subQ5=sQuery(id+"F0.wireOp",EDGE,"E22.filletArc");var subQ6=sQuery(id+"F0.wireOp",EDGE,"E1.bottom");var subQ7=sQuery(id+"F0.wireOp",EDGE,"E1.right");var subQ8=sQuery(id+"F0.wireOp",EDGE,"E1.top");var subQ9=sQuery(id+"F0.wireOp",EDGE,"E1.left");var subQ10=sQuery(id+"F0.wireOp",EDGE,"E23.filletArc");var subQ11=sQuery(id+"F0.wireOp",EDGE,"E24.filletArc");Q0=makeQuery(id+"F2.boolean.opBoolean","SPLIT",FACE,{"disambiguationData":[TD([makeQuery(id+"F1.opExtrude","SWEPT_FACE",FACE,{"disambiguationData":[OSD([subQ6])]})])],"derivedFrom":makeQuery(id+"F1.opExtrude","CAP_FACE",FACE,{"disambiguationData":[OSD([subQ6,subQ8,subQ9,subQ7,subQ4,subQ3,subQ2,subQ1,subQ0,subQ5,subQ10,subQ11])],"isStart":true})});}
            var sketch = newSketch(context, id + "F16", { "sketchPlane" : qUnion([Q0])});
            skLineSegment(sketch, "E79", {"start": v(-33, 74.25) * mm, "end": v(-15, 92.25) * mm});
            skLineSegment(sketch, "E80", {"start": v(33, 74.25) * mm, "end": v(15, 92.25) * mm});
            skLineSegment(sketch, "E81", {"start": v(0, 74.25) * mm, "end": v(0, 104.25) * mm, "construction": true});
            skPoint(sketch, "E82.startSnap0", {"position": v(0, 89.25) * mm});
            skCircle(sketch, "E83", {"center": v(0, 104.25) * mm, "radius": 6 * mm});
            skArc(sketch, "E84", {"start": v(-15, 103.8) * mm, "mid": v(-0.3, 119.25) * mm, "end": v(15, 104.38) * mm});
            skLineSegment(sketch, "E85", {"start": v(-15, 103.8) * mm, "end": v(-15, 92.25) * mm});
            skLineSegment(sketch, "E86", {"start": v(15, 104.38) * mm, "end": v(15, 92.25) * mm});
            skLineSegment(sketch, "E87", {"start": v(-204.24, 0) * mm, "end": v(310.73, 0) * mm, "construction": true});
            skArc(sketch, "E88.MirrorCS", {"start": v(-15, -103.8) * mm, "mid": v(-0.3, -119.25) * mm, "end": v(15, -104.38) * mm});
            skLineSegment(sketch, "E89.MirrorCS", {"start": v(-15, -103.8) * mm, "end": v(-15, -92.25) * mm});
            skLineSegment(sketch, "E90.MirrorCS", {"start": v(-33, -74.25) * mm, "end": v(-15, -92.25) * mm});
            skLineSegment(sketch, "E91.MirrorCS", {"start": v(15, -104.38) * mm, "end": v(15, -92.25) * mm});
            skLineSegment(sketch, "E92.MirrorCS", {"start": v(33, -74.25) * mm, "end": v(15, -92.25) * mm});
            skCircle(sketch, "E93.MirrorC", {"center": v(0, -104.25) * mm, "radius": 6 * mm});
            skSolve(sketch);
        }
        {
            var Q0;
            {var subQ0=sQuery(id+"F16.wireOp",EDGE,"E79");Q0=makeQuery(id+"F16.imprint","IMPRINT",FACE,{"disambiguationData":[TD([[makeQuery(id+"F16.imprint","IMPRINT",EDGE,{"derivedFrom":subQ0}),-1.0]])]});}
            var Q1;
            Q1=makeQuery(id+"F16.imprint","IMPRINT",FACE,{"disambiguationData":[TD([[makeQuery(id+"F16.imprint","IMPRINT",EDGE,{"derivedFrom":makeQuery(id+"F1.opExtrude","CAP_EDGE",EDGE,{"disambiguationData":[OSD([sQuery(id+"F0.wireOp",EDGE,"E1.left")])],"isStart":true})}),-1.0]])]});
            var Q2;
            Q2=makeQuery(id+"F16.imprint","IMPRINT",FACE,{"disambiguationData":[TD([[makeQuery(id+"F16.imprint","IMPRINT",EDGE,{"derivedFrom":sQuery(id+"F16.wireOp",EDGE,"E88.MirrorCS")}),1.0]])]});
            extrude(context, id + "F17", {"entities" : qUnion([Q0, Q1, Q2]), "depth" : 5 * mm, "offsetDistance" : 25 * mm});
        }
    });
